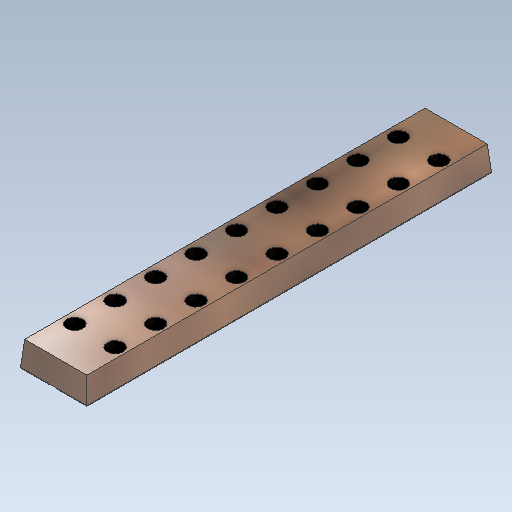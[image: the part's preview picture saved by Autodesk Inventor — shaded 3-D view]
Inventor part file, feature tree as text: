
AUTODESK INVENTOR PART (.ipt)
format: ipt  version: 2021 (Build 250183000, 183)  size: 178,688 bytes
history: native  units: in
note: dims shown in document units (in); Inventor stores cm internally (conversion verified against a paired STEP export)
features: sketch x4, other x3
ambient origin geometry x8: Origin, YZ Plane, XZ Plane, XY Plane, X Axis, Y Axis, Z Axis, Center Point
bodies: Solid1 (feature_tree)
feature tree (7):
  other  "VeroBoardLeadsSIngleHeater.ipt"
  other  "Solid1::VeroBoardLeadsSIngleHeater.ipt"
  other  "TaggingFeature1"
  sketch  "Sketch1"  dims[d0=0.3937in]
  sketch  "Sketch2"  dims[d1=0.12in]
  sketch  "Sketch3"
  sketch  "Sketch4"
